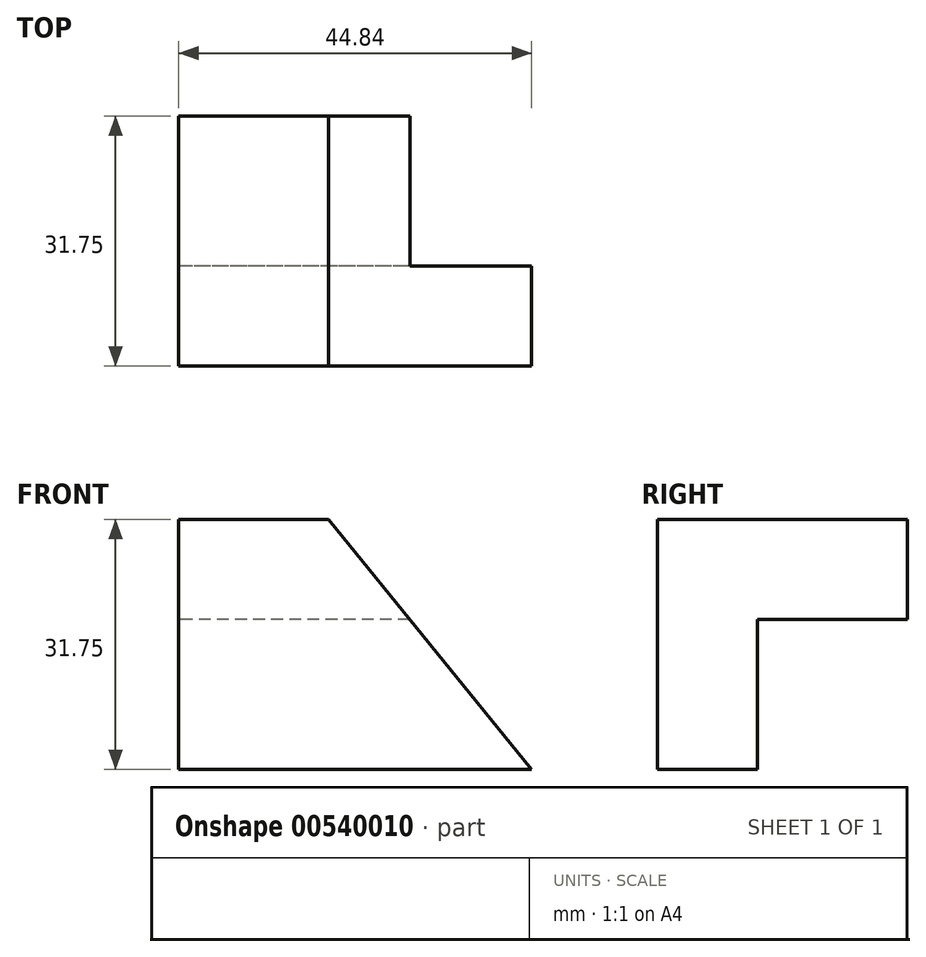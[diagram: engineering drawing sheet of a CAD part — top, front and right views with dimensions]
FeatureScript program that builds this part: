
annotation { "Feature Type Name" : "Feature", "Feature Type Description" : "" }
export const myFeature = defineFeature(function(context is Context, id is Id, definition is map)
    precondition{}
    {
        {
            var Q0;
            Q0=qCreatedBy(makeId("Front.planeOp"),FACE);
            var sketch = newSketch(context, id + "F0", { "sketchPlane" : qUnion([Q0])});
            skLineSegment(sketch, "E0", {"start": v(-70.2, 12.52) * mm, "end": v(-25.35, 12.52) * mm});
            skLineSegment(sketch, "E1", {"start": v(-70.2, 12.52) * mm, "end": v(-70.2, 44.27) * mm});
            skLineSegment(sketch, "E2", {"start": v(-70.2, 44.27) * mm, "end": v(-25.74, 44.27) * mm});
            skLineSegment(sketch, "E3", {"start": v(-25.74, 44.27) * mm, "end": v(-25.35, 12.52) * mm});
            skSolve(sketch);
        }
        {
            var Q0;
            Q0 = qSketchRegion(id + "F0", true);
            extrude(context, id + "F1", {"entities" : qUnion([Q0]), "depth" : 31.75 * mm, "offsetDistance" : 25.4 * mm});
        }
        {
            var Q0;
            Q0=makeQuery(id+"F1.opExtrude","CAP_FACE",FACE,{"disambiguationData":[OSD([sQuery(id+"F0.wireOp",EDGE,"E0"),sQuery(id+"F0.wireOp",EDGE,"E1"),sQuery(id+"F0.wireOp",EDGE,"E2"),sQuery(id+"F0.wireOp",EDGE,"E3")])],"isStart":false});
            var sketch = newSketch(context, id + "F2", { "sketchPlane" : qUnion([Q0])});
            skLineSegment(sketch, "E4", {"start": v(-51.14, 44.27) * mm, "end": v(-25.35, 12.52) * mm});
            skLineSegment(sketch, "E5", {"start": v(-51.14, 44.27) * mm, "end": v(-25.74, 44.27) * mm});
            skLineSegment(sketch, "E6", {"start": v(-25.74, 44.27) * mm, "end": v(-25.35, 12.52) * mm});
            skSolve(sketch);
        }
        {
            var Q0;
            Q0=makeQuery(id+"F2.imprint","IMPRINT",FACE,{"disambiguationData":[TD([[makeQuery(id+"F2.imprint","IMPRINT",EDGE,{"derivedFrom":sQuery(id+"F2.wireOp",EDGE,"E4")}),1.0]])]});
            extrude(context, id + "F3", {"entities" : qUnion([Q0]), "operationType" : NewBodyOperationType.REMOVE, "oppositeDirection" : true, "depth" : 31.75 * mm, "offsetDistance" : 25.4 * mm});
        }
        {
            var Q0;
            Q0=makeQuery(id+"F1.opExtrude","SWEPT_FACE",FACE,{"disambiguationData":[OSD([sQuery(id+"F0.wireOp",EDGE,"E1")])]});
            var sketch = newSketch(context, id + "F4", { "sketchPlane" : qUnion([Q0])});
            skLineSegment(sketch, "E7", {"start": v(0, 12.52) * mm, "end": v(0, 31.57) * mm});
            skLineSegment(sketch, "E8", {"start": v(0, 31.57) * mm, "end": v(19.05, 31.57) * mm});
            skLineSegment(sketch, "E9", {"start": v(19.05, 31.57) * mm, "end": v(19.05, 12.52) * mm});
            skLineSegment(sketch, "E10", {"start": v(19.05, 12.52) * mm, "end": v(0, 12.52) * mm});
            skLineSegment(sketch, "E11", {"start": v(0, 31.57) * mm, "end": v(0, 12.52) * mm});
            skSolve(sketch);
        }
        {
            var Q0;
            Q0 = qSketchRegion(id + "F4", true);
            extrude(context, id + "F5", {"entities" : qUnion([Q0]), "operationType" : NewBodyOperationType.REMOVE, "oppositeDirection" : true, "depth" : 50.8 * mm, "offsetDistance" : 25.4 * mm});
        }
    });
